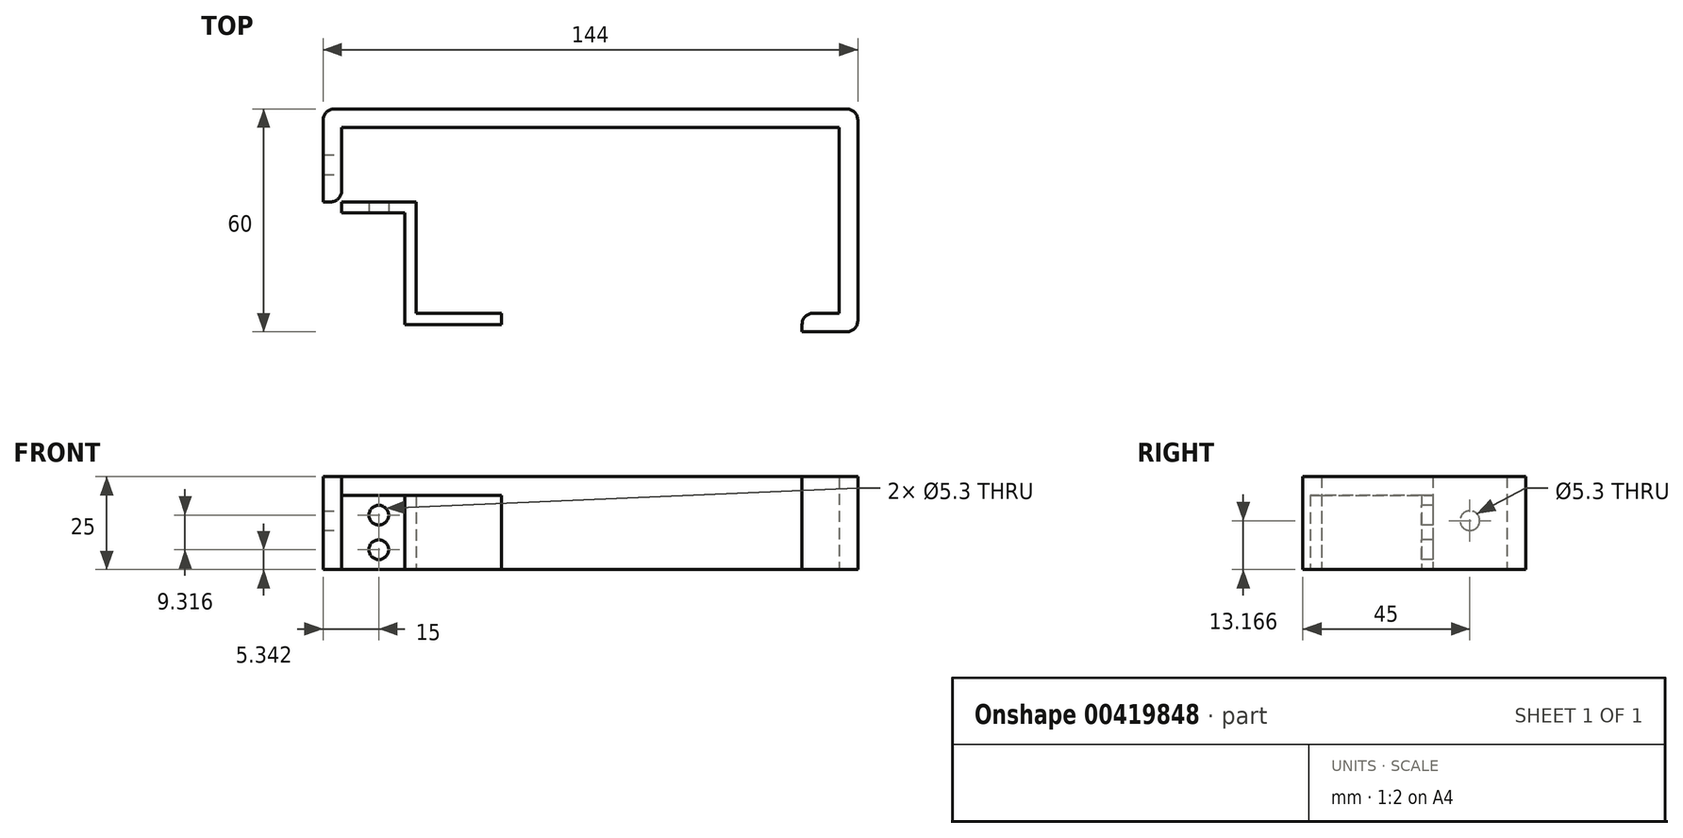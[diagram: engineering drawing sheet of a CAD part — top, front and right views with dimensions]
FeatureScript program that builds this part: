
annotation { "Feature Type Name" : "Feature", "Feature Type Description" : "" }
export const myFeature = defineFeature(function(context is Context, id is Id, definition is map)
    precondition{}
    {
        {
            var Q0;
            Q0=qCreatedBy(makeId("Top.planeOp"),FACE);
            var sketch = newSketch(context, id + "F0", { "sketchPlane" : qUnion([Q0])});
            skLineSegment(sketch, "E0", {"start": v(-54.26, 0) * mm, "end": v(83.74, 0) * mm});
            skLineSegment(sketch, "E1", {"start": v(86.74, -3) * mm, "end": v(86.74, -57) * mm});
            skLineSegment(sketch, "E2", {"start": v(83.74, -60) * mm, "end": v(71.74, -60) * mm});
            skLineSegment(sketch, "E3", {"start": v(71.74, -60) * mm, "end": v(71.74, -58) * mm});
            skLineSegment(sketch, "E4", {"start": v(74.74, -55) * mm, "end": v(81.74, -55) * mm});
            skLineSegment(sketch, "E5", {"start": v(81.74, -55) * mm, "end": v(81.74, -5) * mm});
            skLineSegment(sketch, "E6", {"start": v(81.74, -5) * mm, "end": v(-52.26, -5) * mm});
            skLineSegment(sketch, "E7", {"start": v(-52.26, -5) * mm, "end": v(-52.26, -22) * mm});
            skLineSegment(sketch, "E8", {"start": v(-55.26, -25) * mm, "end": v(-57.26, -25) * mm});
            skLineSegment(sketch, "E9", {"start": v(-57.26, -25) * mm, "end": v(-57.26, -3) * mm});
            skPoint(sketch, "E10.visualSharp", {"position": v(-57.26, 0) * mm});
            skArc(sketch, "E10.filletArc", {"start": v(-54.26, 0) * mm, "mid": v(-56.38, -0.88) * mm, "end": v(-57.26, -3) * mm});
            skPoint(sketch, "E11.visualSharp", {"position": v(86.74, 0) * mm});
            skArc(sketch, "E11.filletArc", {"start": v(86.74, -3) * mm, "mid": v(85.86, -0.88) * mm, "end": v(83.74, 0) * mm});
            skPoint(sketch, "E12.visualSharp", {"position": v(86.74, -60) * mm});
            skArc(sketch, "E12.filletArc", {"start": v(83.74, -60) * mm, "mid": v(85.86, -59.12) * mm, "end": v(86.74, -57) * mm});
            skPoint(sketch, "E13.visualSharp", {"position": v(-52.26, -25) * mm});
            skArc(sketch, "E13.filletArc", {"start": v(-55.26, -25) * mm, "mid": v(-53.14, -24.12) * mm, "end": v(-52.26, -22) * mm});
            skPoint(sketch, "E14.visualSharp", {"position": v(71.74, -55) * mm});
            skArc(sketch, "E14.filletArc", {"start": v(74.74, -55) * mm, "mid": v(72.62, -55.88) * mm, "end": v(71.74, -58) * mm});
            skSolve(sketch);
        }
        {
            var Q0;
            Q0 = qSketchRegion(id + "F0", true);
            extrude(context, id + "F1", {"entities" : qUnion([Q0]), "depth" : 25 * mm});
        }
        {
            var Q0;
            Q0=makeQuery(id+"F1.opExtrude","SWEPT_FACE",FACE,{"disambiguationData":[OSD([sQuery(id+"F0.wireOp",EDGE,"E7")])]});
            var sketch = newSketch(context, id + "F2", { "sketchPlane" : qUnion([Q0])});
            skCircle(sketch, "E15", {"center": v(-15, 13.17) * mm, "radius": 2.65 * mm});
            skSolve(sketch);
        }
        {
            var Q0;
            Q0 = qSketchRegion(id + "F2", true);
            extrude(context, id + "F3", {"entities" : qUnion([Q0]), "operationType" : NewBodyOperationType.REMOVE, "endBound" : BoundingType.UP_TO_NEXT, "oppositeDirection" : true, "depth" : 25 * mm});
        }
        {
            var Q0;
            Q0=qCreatedBy(makeId("Front.planeOp"),FACE);
            cPlane(context, id + "F4", {"entities" : qUnion([Q0]), "cplaneType" : CPlaneType.OFFSET, "offset" : 60.9 * mm, "width" : 150 * mm, "height" : 150 * mm});
        }
        {
            var Q0;
            Q0=qCreatedBy(id+"F4.planeOp",FACE);
            var sketch = newSketch(context, id + "F5", { "sketchPlane" : qUnion([Q0])});
            skLineSegment(sketch, "E16.bottom", {"start": v(-57.21, 0) * mm, "end": v(-17.21, 0) * mm});
            skLineSegment(sketch, "E16.top", {"start": v(-57.21, 20) * mm, "end": v(-17.21, 20) * mm});
            skLineSegment(sketch, "E16.left", {"start": v(-57.21, 0) * mm, "end": v(-57.21, 20) * mm});
            skLineSegment(sketch, "E16.right", {"start": v(-17.21, 0) * mm, "end": v(-17.21, 20) * mm});
            skCircle(sketch, "E17", {"center": v(-47.21, 14.99) * mm, "radius": 2.65 * mm});
            skCircle(sketch, "E18", {"center": v(-47.21, 5.01) * mm, "radius": 2.65 * mm});
            skLineSegment(sketch, "E19", {"start": v(-47.32, 20) * mm, "end": v(-47.32, 17.64) * mm, "construction": true});
            skLineSegment(sketch, "E20", {"start": v(-47.27, 2.36) * mm, "end": v(-47.27, 0) * mm, "construction": true});
            skLineSegment(sketch, "E21", {"start": v(-47.13, 12.34) * mm, "end": v(-47.13, 7.66) * mm, "construction": true});
            skSolve(sketch);
        }
        {
            var Q0;
            Q0 = qSketchRegion(id + "F5", true);
            extrude(context, id + "F6", {"entities" : qUnion([Q0]), "depth" : 3 * mm});
        }
        {
            var Q0;
            Q0=makeQuery(id+"F6.opExtrude","CAP_EDGE",EDGE,{"disambiguationData":[OSD([sQuery(id+"F5.wireOp",EDGE,"E16.top")])],"isStart":false});
            var Q1;
            Q1=makeQuery(id+"F6.opExtrude","CAP_EDGE",EDGE,{"disambiguationData":[OSD([sQuery(id+"F5.wireOp",EDGE,"E16.top")])],"isStart":true});
            var Q2;
            Q2=makeQuery(id+"F6.opExtrude","CAP_EDGE",EDGE,{"disambiguationData":[OSD([sQuery(id+"F5.wireOp",EDGE,"E16.bottom")])],"isStart":false});
            var Q3;
            Q3=makeQuery(id+"F6.opExtrude","CAP_EDGE",EDGE,{"disambiguationData":[OSD([sQuery(id+"F5.wireOp",EDGE,"E16.bottom")])],"isStart":true});
            var Q4;
            Q4=makeQuery(id+"F6.opExtrude","CAP_EDGE",EDGE,{"disambiguationData":[OSD([sQuery(id+"F5.wireOp",EDGE,"E16.right")])],"isStart":false});
            var Q5;
            Q5=makeQuery(id+"F6.opExtrude","CAP_EDGE",EDGE,{"disambiguationData":[OSD([sQuery(id+"F5.wireOp",EDGE,"E16.right")])],"isStart":true});
            var Q6;
            Q6=makeQuery(id+"F6.opExtrude","CAP_EDGE",EDGE,{"disambiguationData":[OSD([sQuery(id+"F5.wireOp",EDGE,"E16.left")])],"isStart":false});
            var Q7;
            Q7=makeQuery(id+"F6.opExtrude","CAP_EDGE",EDGE,{"disambiguationData":[OSD([sQuery(id+"F5.wireOp",EDGE,"E16.left")])],"isStart":true});
            fillet(context, id + "F7", {"entities" : qUnion([Q0, Q1, Q2, Q3, Q4, Q5, Q6, Q7]), "radius" : 1 * mm, "tangentPropagation" : true, "allowEdgeOverflow" : false});
        }
        {
            var Q0;
            Q0=makeQuery(id+"F6.opExtrude","SWEPT_BODY",BODY,{"disambiguationData":[OSD([sQuery(id+"F5.wireOp",EDGE,"E16.bottom"),sQuery(id+"F5.wireOp",EDGE,"E16.top"),sQuery(id+"F5.wireOp",EDGE,"E16.left"),sQuery(id+"F5.wireOp",EDGE,"E16.right"),sQuery(id+"F5.wireOp",EDGE,"E17"),sQuery(id+"F5.wireOp",EDGE,"E18")])]});
            deleteBodies(context, id + "F8", {"entities" : qUnion([Q0])});
        }
        {
            var Q0;
            Q0=qCreatedBy(makeId("Top.planeOp"),FACE);
            var sketch = newSketch(context, id + "F9", { "sketchPlane" : qUnion([Q0])});
            skLineSegment(sketch, "E22.bottom", {"start": v(-52.26, -5) * mm, "end": v(-32.26, -5) * mm, "construction": true});
            skLineSegment(sketch, "E22.top", {"start": v(-52.26, -25) * mm, "end": v(-32.26, -25) * mm, "construction": true});
            skLineSegment(sketch, "E22.left", {"start": v(-52.26, -5) * mm, "end": v(-52.26, -25) * mm, "construction": true});
            skLineSegment(sketch, "E22.right", {"start": v(-32.26, -5) * mm, "end": v(-32.26, -25) * mm, "construction": true});
            skLineSegment(sketch, "E23", {"start": v(-52.26, -25) * mm, "end": v(-52.26, -28) * mm});
            skLineSegment(sketch, "E24", {"start": v(-9.26, -58) * mm, "end": v(-9.26, -55) * mm});
            skLineSegment(sketch, "E25", {"start": v(-32.26, -54.96) * mm, "end": v(-32.26, -25) * mm});
            skLineSegment(sketch, "E26", {"start": v(-52.26, -25) * mm, "end": v(-32.26, -25) * mm});
            skLineSegment(sketch, "E27", {"start": v(-32.26, -54.96) * mm, "end": v(-9.26, -55) * mm});
            skLineSegment(sketch, "E28", {"start": v(-26.3, -55.04) * mm, "end": v(-32.26, -54.96) * mm});
            skLineSegment(sketch, "E29", {"start": v(-52.26, -28) * mm, "end": v(-35.26, -28) * mm});
            skLineSegment(sketch, "E30", {"start": v(-35.26, -28) * mm, "end": v(-35.26, -58) * mm});
            skLineSegment(sketch, "E31", {"start": v(-35.26, -58) * mm, "end": v(-9.26, -58) * mm});
            skSolve(sketch);
        }
        {
            var Q0;
            Q0 = qSketchRegion(id + "F9", true);
            extrude(context, id + "F10", {"entities" : qUnion([Q0]), "depth" : 20 * mm});
        }
        {
            var Q0;
            Q0=makeQuery(id+"F10.opExtrude","SWEPT_FACE",FACE,{"disambiguationData":[OSD([sQuery(id+"F9.wireOp",EDGE,"E29")])]});
            var sketch = newSketch(context, id + "F11", { "sketchPlane" : qUnion([Q0])});
            skCircle(sketch, "E32", {"center": v(-42.26, 14.66) * mm, "radius": 2.65 * mm});
            skCircle(sketch, "E33", {"center": v(-42.26, 5.34) * mm, "radius": 2.65 * mm});
            skLineSegment(sketch, "E34", {"start": v(-42.26, 14.66) * mm, "end": v(-42.26, 20) * mm, "construction": true});
            skLineSegment(sketch, "E35", {"start": v(-42.26, 5.34) * mm, "end": v(-42.26, 0) * mm, "construction": true});
            skSolve(sketch);
        }
        {
            var Q0;
            Q0 = qSketchRegion(id + "F11", true);
            extrude(context, id + "F12", {"entities" : qUnion([Q0]), "operationType" : NewBodyOperationType.REMOVE, "endBound" : BoundingType.UP_TO_NEXT, "oppositeDirection" : true, "depth" : 25 * mm});
        }
    });
